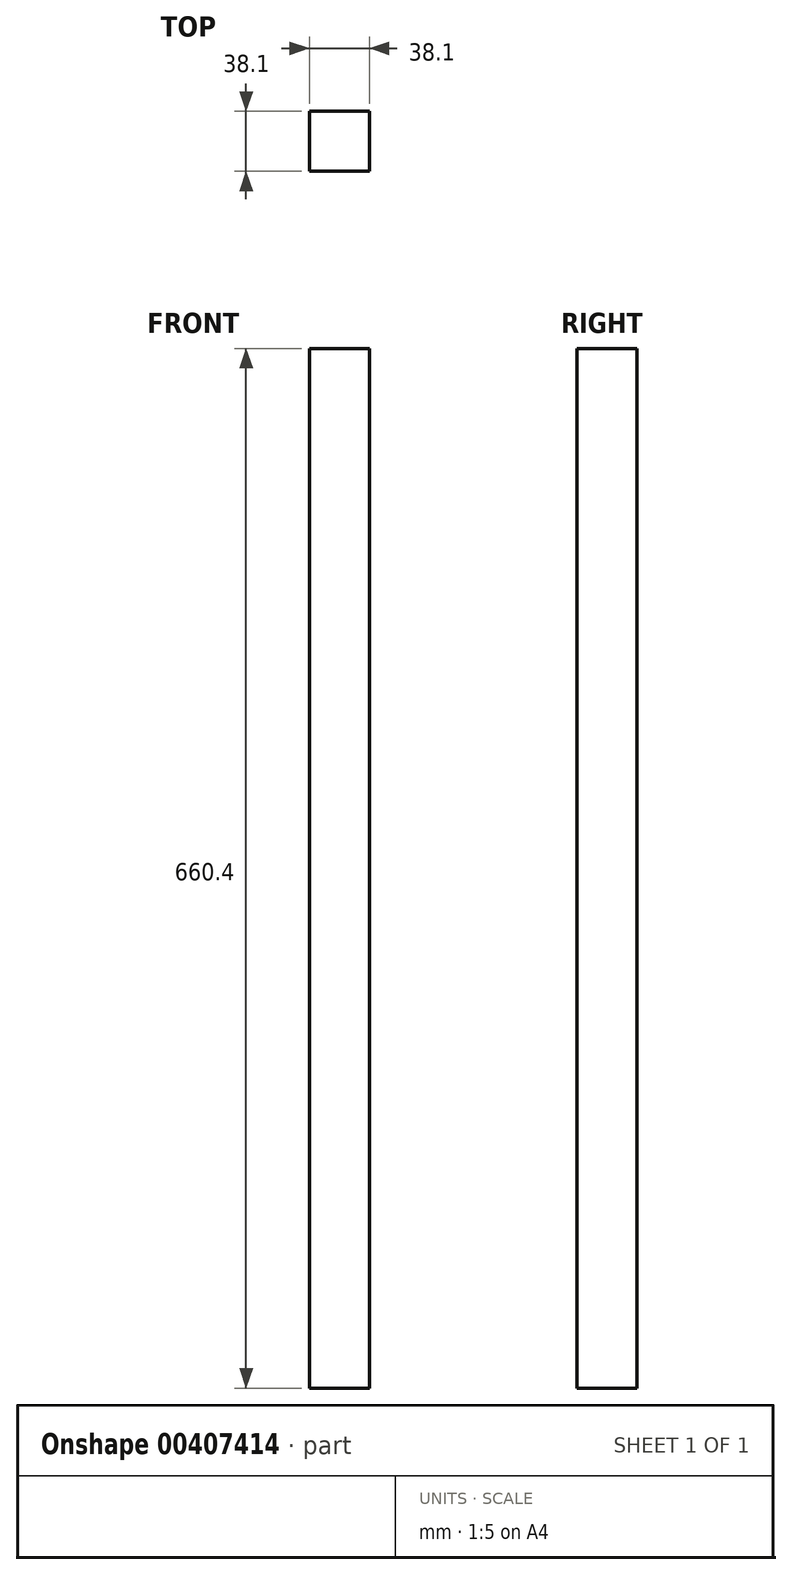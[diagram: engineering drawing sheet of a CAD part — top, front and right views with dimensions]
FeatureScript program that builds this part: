
annotation { "Feature Type Name" : "Feature", "Feature Type Description" : "" }
export const myFeature = defineFeature(function(context is Context, id is Id, definition is map)
    precondition{}
    {
        {
            var Q0;
            Q0=qCreatedBy(makeId("Top.planeOp"),FACE);
            var sketch = newSketch(context, id + "F0", { "sketchPlane" : qUnion([Q0])});
            skLineSegment(sketch, "E0.bottom", {"start": v(19.05, 19.05) * mm, "end": v(-19.05, 19.05) * mm});
            skLineSegment(sketch, "E0.top", {"start": v(19.05, -19.05) * mm, "end": v(-19.05, -19.05) * mm});
            skLineSegment(sketch, "E0.left", {"start": v(19.05, 19.05) * mm, "end": v(19.05, -19.05) * mm});
            skLineSegment(sketch, "E0.right", {"start": v(-19.05, 19.05) * mm, "end": v(-19.05, -19.05) * mm});
            skPoint(sketch, "E0.middle", {"position": v(0, 0) * mm});
            skSolve(sketch);
        }
        {
            var Q0;
            Q0=makeQuery(id+"F0.imprint","IMPRINT",FACE,{"disambiguationData":[TD([[makeQuery(id+"F0.imprint","IMPRINT",EDGE,{"derivedFrom":sQuery(id+"F0.wireOp",EDGE,"E0.bottom")}),1.0]])]});
            extrude(context, id + "F1", {"entities" : qUnion([Q0]), "depth" : 660.4 * mm});
        }
    });
